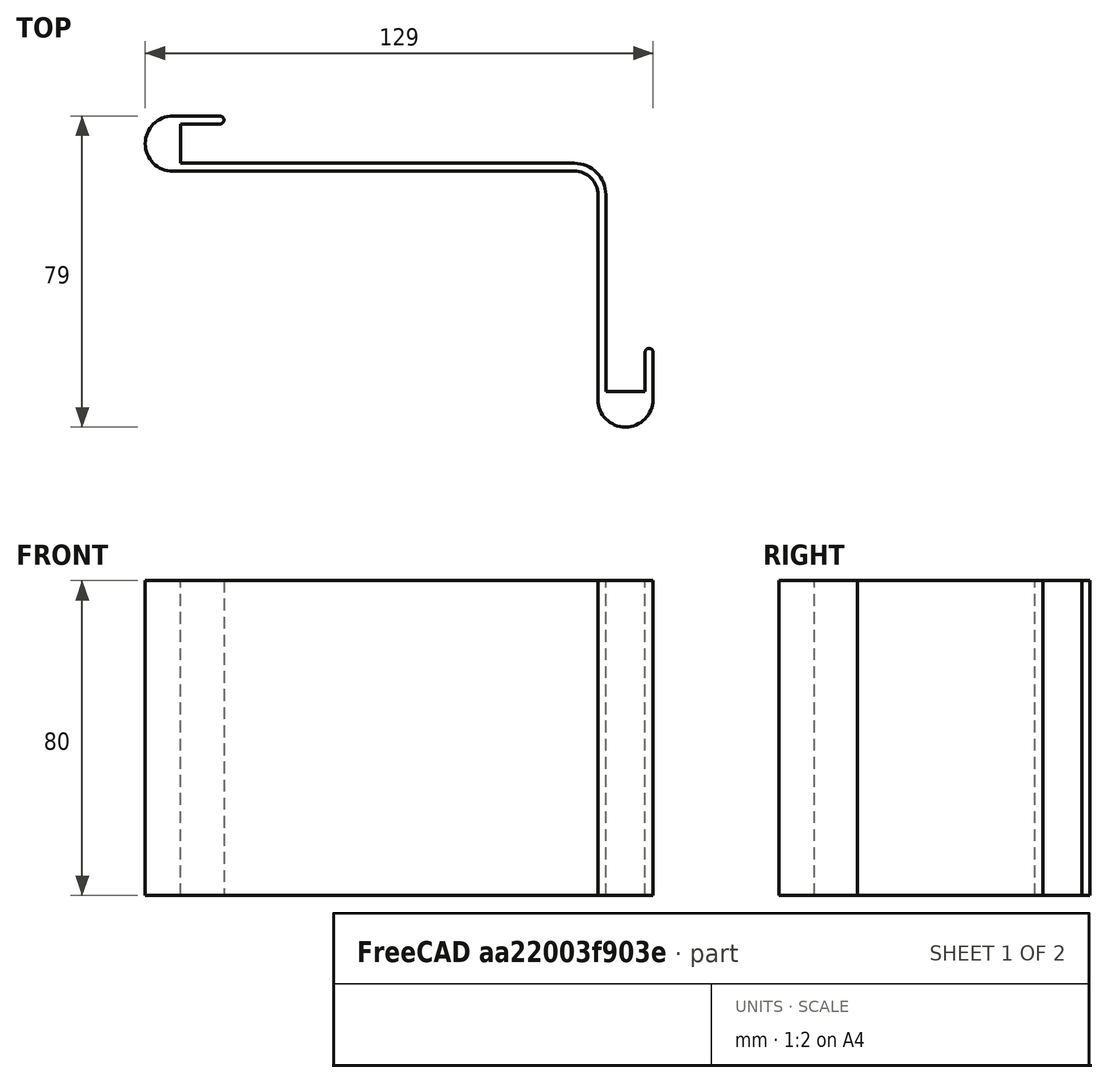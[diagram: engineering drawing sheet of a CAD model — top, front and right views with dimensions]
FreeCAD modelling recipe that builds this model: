
FCSTD DOCUMENT  (FreeCAD 0.16R6712 (Git))
Label: Support tablette
License: All rights reserved
LicenseURL: http://en.wikipedia.org/wiki/All_rights_reserved
objects: Sketcher::SketchObject×1, PartDesign::Pad×1
note: 3 computed .brp shape members not serialized (recipe doc carries the construction recipe); baked Part::Feature solids carry a one-line shape summary decoded from their .brp

FEATURE [Sketcher::SketchObject] Sketch
  sketch-geometry (21):
    g0: LineSegment StartX=-53.4419 StartY=0 StartZ=0 EndX=46.5581 EndY=0 EndZ=0
    g1: LineSegment StartX=-53.4419 StartY=0 StartZ=0 EndX=-53.4419 EndY=10 EndZ=0
    g2: LineSegment StartX=-53.4419 StartY=10 StartZ=0 EndX=-43.4419 EndY=10 EndZ=0
    g3: LineSegment [constr] StartX=-43.4419 StartY=10 StartZ=0 EndX=-43.4419 EndY=12 EndZ=0
    g4: LineSegment StartX=-43.4419 StartY=12 StartZ=0 EndX=-55.4419 EndY=12 EndZ=0
    g5: LineSegment [constr] StartX=-55.4419 StartY=12 StartZ=0 EndX=-55.4419 EndY=-2 EndZ=0
    g6: LineSegment StartX=-55.4419 StartY=-2 StartZ=0 EndX=46.5581 EndY=-2 EndZ=0
    g7: LineSegment StartX=52.5581 StartY=-8 StartZ=0 EndX=52.5581 EndY=-60 EndZ=0
    g8: LineSegment [constr] StartX=52.5581 StartY=-60 StartZ=0 EndX=66.5581 EndY=-60 EndZ=0
    g9: LineSegment StartX=66.5581 StartY=-60 StartZ=0 EndX=66.5581 EndY=-48 EndZ=0
    g10: LineSegment [constr] StartX=66.5581 StartY=-48 StartZ=0 EndX=64.5581 EndY=-48 EndZ=0
    g11: LineSegment StartX=64.5581 StartY=-48 StartZ=0 EndX=64.5581 EndY=-58 EndZ=0
    g12: LineSegment StartX=64.5581 StartY=-58 StartZ=0 EndX=54.5581 EndY=-58 EndZ=0
    g13: LineSegment StartX=54.5581 StartY=-58 StartZ=0 EndX=54.5581 EndY=-8 EndZ=0
    g14: ArcOfCircle CenterX=59.5581 CenterY=-60 CenterZ=0 NormalX=0 NormalY=0 NormalZ=1 Radius=7 StartAngle=3.14159 EndAngle=6.28319
    g15: ArcOfCircle CenterX=-55.4419 CenterY=5 CenterZ=0 NormalX=0 NormalY=0 NormalZ=1 Radius=7 StartAngle=1.5708 EndAngle=4.71239
    g16: ArcOfCircle CenterX=46.5581 CenterY=-8 CenterZ=0 NormalX=0 NormalY=0 NormalZ=1 Radius=6 StartAngle=0 EndAngle=1.5708
    g17: ArcOfCircle CenterX=46.5581 CenterY=-8 CenterZ=0 NormalX=0 NormalY=0 NormalZ=1 Radius=8 StartAngle=0 EndAngle=1.5708
    g18: LineSegment [constr] StartX=46.5581 StartY=0 StartZ=0 EndX=46.5581 EndY=-2 EndZ=0
    g19: ArcOfCircle CenterX=65.5581 CenterY=-48 CenterZ=0 NormalX=0 NormalY=0 NormalZ=1 Radius=1 StartAngle=0 EndAngle=3.14159
    g20: ArcOfCircle CenterX=-43.4419 CenterY=11 CenterZ=0 NormalX=0 NormalY=0 NormalZ=1 Radius=1 StartAngle=4.71239 EndAngle=7.85398
  constraints (59):
    c: Horizontal(g0)
    c: Coincident(g0,g1)
    c: Coincident(g1,g2)
    c: Coincident(g2,g3)
    c: Vertical(g3)
    c: Coincident(g3,g4)
    c: Horizontal(g4)
    c: Coincident(g4,g5)
    c: Vertical(g5)
    c: Coincident(g5,g6)
    c: Horizontal(g6)
    c: Vertical(g7)
    c: Coincident(g7,g8)
    c: Horizontal(g8)
    c: Coincident(g8,g9)
    c: Vertical(g9)
    c: Coincident(g9,g10)
    c: Horizontal(g10)
    c: Coincident(g10,g11)
    c: Coincident(g11,g12)
    c: Horizontal(g12)
    c: Coincident(g12,g13)
    c: Vertical(g13)
    c: Vertical(g1)
    c: DistanceY(g0,g1) = 10
    c: Horizontal(g2)
    c: DistanceY(g2,g3) = 2
    c: DistanceX(g5,g0) = 2
    c: DistanceY(g5,g0) = 2
    c: DistanceY(g7,g12) = 2
    c: DistanceX(g12,g11) = 10
    c: Vertical(g11)
    c: DistanceX(g10,g9) = 2
    c: DistanceY(g11,g10) = 10
    c: DistanceX(g1,g2) = 10
    c: PointOnObject(g-1,g0)
    c: PointOnObject(g14,g8)
    c: Coincident(g14,g7)
    c: Coincident(g14,g8)
    c: PointOnObject(g15,g5)
    c: Coincident(g15,g5)
    c: Coincident(g15,g4)
    c: Tangent(g6,g16) = 1.5708
    c: Tangent(g7,g16) = 1.5708
    c: Tangent(g0,g17) = 1.5708
    c: Tangent(g13,g17) = -1.5708
    c: DistanceX(g0,g0) = 100
    c: DistanceY(g12,g13) = 50
    c: DistanceX(g7,g12) = 2
    c: DistanceY(g16,g6) = 6
    c: Coincident(g18,g0)
    c: Coincident(g18,g6)
    c: Vertical(g18)
    c: PointOnObject(g19,g10)
    c: Coincident(g19,g9)
    c: Coincident(g19,g10)
    c: PointOnObject(g20,g3)
    c: Coincident(g20,g3)
    c: Coincident(g20,g2)
FEATURE [PartDesign::Pad] Pad
  Length = 80
  Length2 = 100
  Sketch = -> Sketch
  Type = 0
